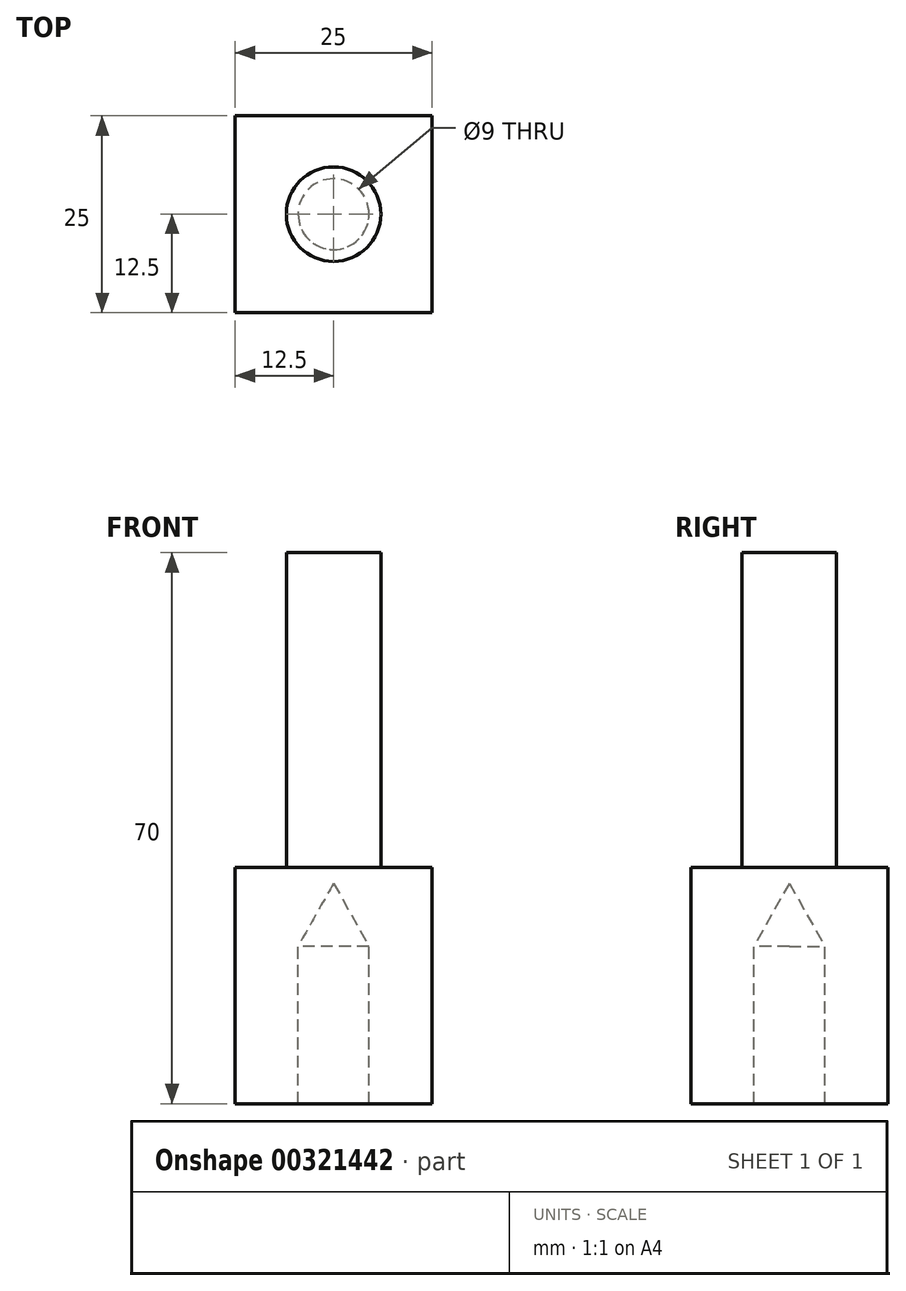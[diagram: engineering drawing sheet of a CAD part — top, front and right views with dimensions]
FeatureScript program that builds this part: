
annotation { "Feature Type Name" : "Feature", "Feature Type Description" : "" }
export const myFeature = defineFeature(function(context is Context, id is Id, definition is map)
    precondition{}
    {
        {
            var Q0;
            Q0=qCreatedBy(makeId("Top.planeOp"),FACE);
            var sketch = newSketch(context, id + "F0", { "sketchPlane" : qUnion([Q0])});
            skLineSegment(sketch, "E0.bottom", {"start": v(12.5, -12.5) * mm, "end": v(-12.5, -12.5) * mm});
            skLineSegment(sketch, "E0.top", {"start": v(12.5, 12.5) * mm, "end": v(-12.5, 12.5) * mm});
            skLineSegment(sketch, "E0.left", {"start": v(12.5, -12.5) * mm, "end": v(12.5, 12.5) * mm});
            skLineSegment(sketch, "E0.right", {"start": v(-12.5, -12.5) * mm, "end": v(-12.5, 12.5) * mm});
            skPoint(sketch, "E0.middle", {"position": v(0, 0) * mm});
            skSolve(sketch);
        }
        {
            var Q0;
            Q0 = qSketchRegion(id + "F0", true);
            extrude(context, id + "F1", {"entities" : qUnion([Q0]), "depth" : 10 * mm});
        }
        {
            var Q0;
            Q0=qCreatedBy(makeId("Front.planeOp"),FACE);
            var sketch = newSketch(context, id + "F2", { "sketchPlane" : qUnion([Q0])});
            skLineSegment(sketch, "E1", {"start": v(0, 8) * mm, "end": v(4.5, 0) * mm});
            skLineSegment(sketch, "E2", {"start": v(0, 8) * mm, "end": v(0, 0) * mm});
            skLineSegment(sketch, "E3", {"start": v(0, 0) * mm, "end": v(4.5, 0) * mm});
            skSolve(sketch);
        }
        {
            var Q0;
            Q0=makeQuery(id+"F2.imprint","IMPRINT",FACE,{"disambiguationData":[TD([[makeQuery(id+"F2.imprint","IMPRINT",EDGE,{"derivedFrom":sQuery(id+"F2.wireOp",EDGE,"E1")}),-1.0]])]});
            var Q1;
            Q1=sQuery(id+"F2.wireOp",EDGE,"E2");
            revolve(context, id + "F3", {"operationType" : NewBodyOperationType.REMOVE, "entities" : qUnion([Q0]), "axis" : qUnion([Q1]), "revolveType" : RevolveType.FULL, "oppositeDirection" : true});
        }
        {
            var Q0;
            Q0=qCreatedBy(makeId("Top.planeOp"),FACE);
            var sketch = newSketch(context, id + "F4", { "sketchPlane" : qUnion([Q0])});
            skLineSegment(sketch, "E4.bottom", {"start": v(12.5, 12.5) * mm, "end": v(-12.5, 12.5) * mm});
            skLineSegment(sketch, "E4.top", {"start": v(12.5, -12.5) * mm, "end": v(-12.5, -12.5) * mm});
            skLineSegment(sketch, "E4.left", {"start": v(12.5, 12.5) * mm, "end": v(12.5, -12.5) * mm});
            skLineSegment(sketch, "E4.right", {"start": v(-12.5, 12.5) * mm, "end": v(-12.5, -12.5) * mm});
            skPoint(sketch, "E4.middle", {"position": v(0, 0) * mm});
            skCircle(sketch, "E5", {"center": v(0, 0) * mm, "radius": 4.5 * mm});
            skSolve(sketch);
        }
        {
            var Q0;
            Q0 = qSketchRegion(id + "F4", true);
            extrude(context, id + "F5", {"entities" : qUnion([Q0]), "operationType" : NewBodyOperationType.ADD, "oppositeDirection" : true, "depth" : 20 * mm});
        }
        {
            var Q0;
            Q0=makeQuery(id+"F1.opExtrude","CAP_FACE",FACE,{"disambiguationData":[OSD([sQuery(id+"F0.wireOp",EDGE,"E0.bottom"),sQuery(id+"F0.wireOp",EDGE,"E0.top"),sQuery(id+"F0.wireOp",EDGE,"E0.left"),sQuery(id+"F0.wireOp",EDGE,"E0.right")])],"isStart":false});
            var sketch = newSketch(context, id + "F6", { "sketchPlane" : qUnion([Q0])});
            skCircle(sketch, "E6", {"center": v(0, 0) * mm, "radius": 6 * mm});
            skSolve(sketch);
        }
        {
            var Q0;
            Q0 = qSketchRegion(id + "F6", true);
            extrude(context, id + "F7", {"entities" : qUnion([Q0]), "operationType" : NewBodyOperationType.ADD, "depth" : 40 * mm});
        }
    });
